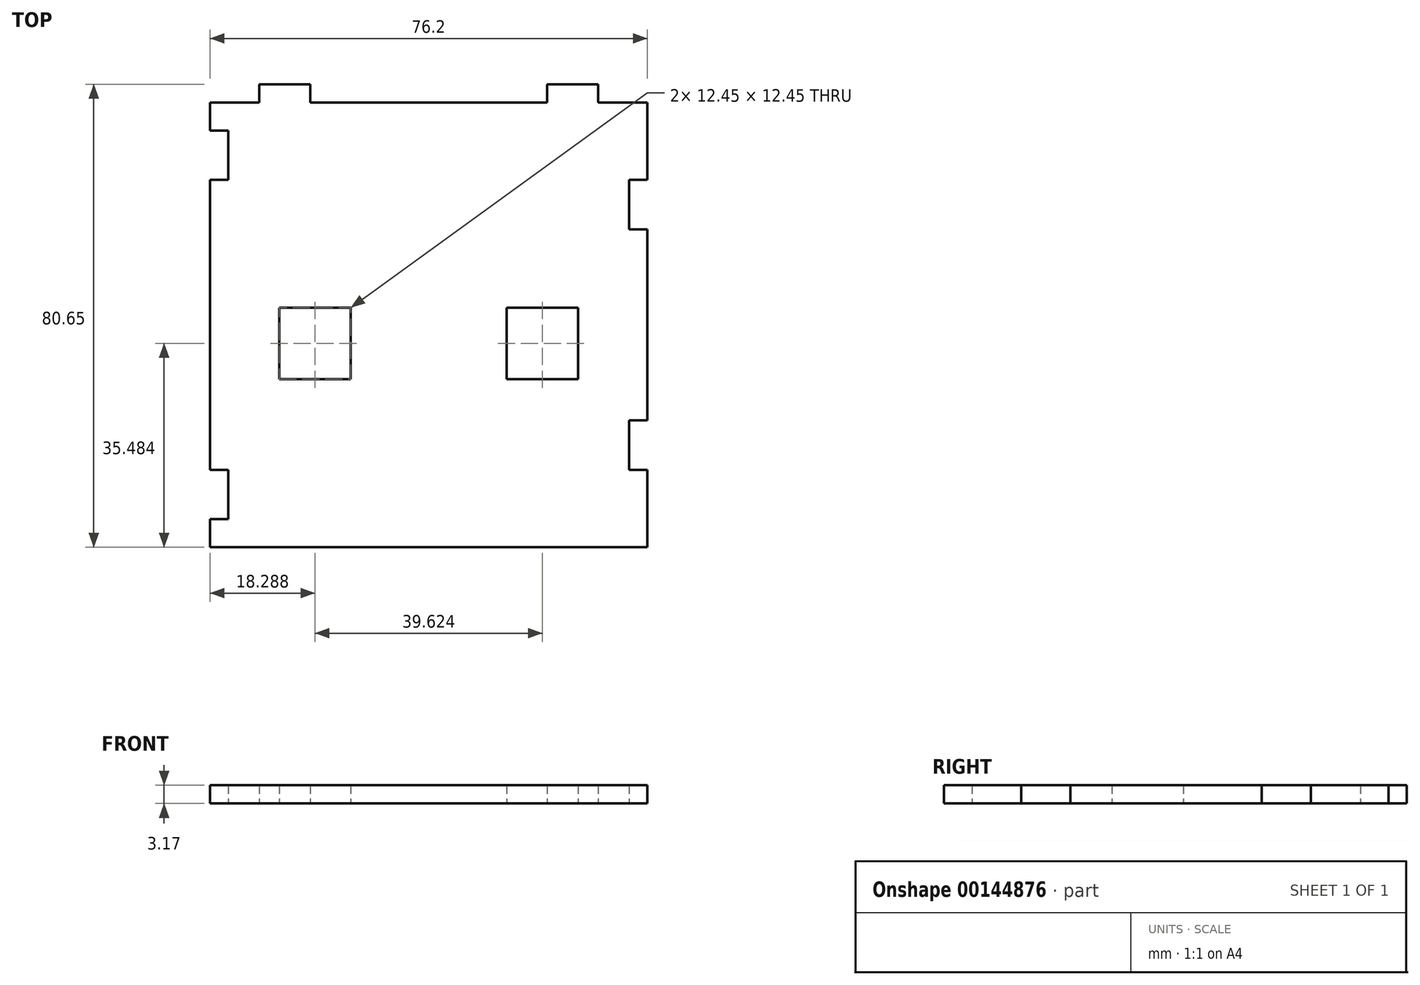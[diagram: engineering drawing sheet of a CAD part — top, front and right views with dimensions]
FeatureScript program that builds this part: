
annotation { "Feature Type Name" : "Feature", "Feature Type Description" : "" }
export const myFeature = defineFeature(function(context is Context, id is Id, definition is map)
    precondition{}
    {
        {
            var Q0;
            Q0=qCreatedBy(makeId("Top.planeOp"),FACE);
            var sketch = newSketch(context, id + "F0", { "sketchPlane" : qUnion([Q0])});
            skLineSegment(sketch, "E0.bottom", {"start": v(-38.1, 41.91) * mm, "end": v(38.1, 41.91) * mm});
            skLineSegment(sketch, "E0.top", {"start": v(-38.1, -35.56) * mm, "end": v(38.1, -35.56) * mm});
            skLineSegment(sketch, "E0.left", {"start": v(-38.1, 41.91) * mm, "end": v(-38.1, -35.56) * mm});
            skLineSegment(sketch, "E0.right", {"start": v(38.1, 41.91) * mm, "end": v(38.1, -35.56) * mm});
            skPoint(sketch, "E1", {"position": v(-29.53, 41.91) * mm});
            skPoint(sketch, "E2", {"position": v(-20.64, 41.91) * mm});
            skPoint(sketch, "E3", {"position": v(0.15, 41.91) * mm});
            skPoint(sketch, "E4", {"position": v(0, 41.91) * mm});
            skPoint(sketch, "E5", {"position": v(20.62, 41.91) * mm});
            skPoint(sketch, "E6", {"position": v(29.51, 41.91) * mm});
            skLineSegment(sketch, "E7", {"start": v(0.15, 41.91) * mm, "end": v(-4.3, 41.91) * mm});
            skPoint(sketch, "E8", {"position": v(4.6, 41.91) * mm});
            skLineSegment(sketch, "E9", {"start": v(0.15, 41.91) * mm, "end": v(4.6, 41.91) * mm});
            skPoint(sketch, "E10", {"position": v(-29.53, -35.56) * mm});
            skPoint(sketch, "E11", {"position": v(-20.64, -35.56) * mm});
            skPoint(sketch, "E12", {"position": v(-4.3, -35.56) * mm});
            skPoint(sketch, "E13", {"position": v(4.6, -35.56) * mm});
            skPoint(sketch, "E14", {"position": v(20.62, -35.56) * mm});
            skPoint(sketch, "E15", {"position": v(29.51, -35.56) * mm});
            skLineSegment(sketch, "E16.bottom", {"start": v(20.62, -35.56) * mm, "end": v(29.2, -35.56) * mm});
            skPoint(sketch, "E17", {"position": v(38.1, 24.13) * mm});
            skPoint(sketch, "E18", {"position": v(38.1, -17.78) * mm});
            skPoint(sketch, "E19", {"position": v(38.1, 3.18) * mm});
            skPoint(sketch, "E20", {"position": v(38.1, 28.42) * mm});
            skPoint(sketch, "E21", {"position": v(38.1, 19.84) * mm});
            skPoint(sketch, "E22", {"position": v(38.1, -13.49) * mm});
            skPoint(sketch, "E23", {"position": v(38.1, -22.07) * mm});
            skLineSegment(sketch, "E24.bottom", {"start": v(38.1, 28.42) * mm, "end": v(34.93, 28.42) * mm});
            skLineSegment(sketch, "E24.top", {"start": v(38.1, 19.84) * mm, "end": v(34.93, 19.84) * mm});
            skLineSegment(sketch, "E24.left", {"start": v(38.1, 28.42) * mm, "end": v(38.1, 19.84) * mm});
            skLineSegment(sketch, "E24.right", {"start": v(34.93, 28.42) * mm, "end": v(34.93, 19.84) * mm});
            skLineSegment(sketch, "E25.bottom", {"start": v(38.1, -13.49) * mm, "end": v(34.93, -13.49) * mm});
            skLineSegment(sketch, "E25.top", {"start": v(38.1, -22.07) * mm, "end": v(34.93, -22.07) * mm});
            skLineSegment(sketch, "E25.left", {"start": v(38.1, -13.49) * mm, "end": v(38.1, -22.07) * mm});
            skLineSegment(sketch, "E25.right", {"start": v(34.93, -13.49) * mm, "end": v(34.93, -22.07) * mm});
            skLineSegment(sketch, "E26.bottom", {"start": v(-38.1, 28.42) * mm, "end": v(-34.92, 28.42) * mm});
            skLineSegment(sketch, "E26.top", {"start": v(-38.1, 37) * mm, "end": v(-34.92, 37) * mm});
            skLineSegment(sketch, "E26.left", {"start": v(-38.1, 28.42) * mm, "end": v(-38.1, 37) * mm});
            skLineSegment(sketch, "E26.right", {"start": v(-34.92, 28.42) * mm, "end": v(-34.92, 37) * mm});
            skLineSegment(sketch, "E27.bottom", {"start": v(-38.1, -22.07) * mm, "end": v(-34.92, -22.07) * mm});
            skLineSegment(sketch, "E27.top", {"start": v(-38.1, -30.66) * mm, "end": v(-34.92, -30.66) * mm});
            skLineSegment(sketch, "E27.left", {"start": v(-38.1, -22.07) * mm, "end": v(-38.1, -30.66) * mm});
            skLineSegment(sketch, "E27.right", {"start": v(-34.93, -22.07) * mm, "end": v(-34.93, -30.66) * mm});
            skLineSegment(sketch, "E28.top", {"start": v(-29.53, 45.09) * mm, "end": v(-20.64, 45.09) * mm});
            skLineSegment(sketch, "E28.left", {"start": v(-29.53, 41.91) * mm, "end": v(-29.53, 45.09) * mm});
            skLineSegment(sketch, "E28.right", {"start": v(-20.64, 41.91) * mm, "end": v(-20.64, 45.09) * mm});
            skLineSegment(sketch, "E29.top", {"start": v(20.62, 45.09) * mm, "end": v(29.51, 45.09) * mm});
            skLineSegment(sketch, "E29.left", {"start": v(20.62, 41.91) * mm, "end": v(20.62, 45.09) * mm});
            skLineSegment(sketch, "E29.right", {"start": v(29.51, 41.91) * mm, "end": v(29.51, 45.09) * mm});
            skLineSegment(sketch, "E30.top", {"start": v(-4.3, 45.09) * mm, "end": v(4.6, 45.09) * mm});
            skLineSegment(sketch, "E30.left", {"start": v(-4.3, 41.91) * mm, "end": v(-4.3, 45.09) * mm});
            skLineSegment(sketch, "E30.right", {"start": v(4.6, 41.91) * mm, "end": v(4.6, 45.09) * mm});
            skLineSegment(sketch, "E31.bottom", {"start": v(-29.53, -35.56) * mm, "end": v(-20.64, -35.56) * mm});
            skLineSegment(sketch, "E31.top", {"start": v(-29.53, -38.73) * mm, "end": v(-20.64, -38.73) * mm});
            skLineSegment(sketch, "E31.left", {"start": v(-29.53, -35.56) * mm, "end": v(-29.53, -38.73) * mm});
            skLineSegment(sketch, "E31.right", {"start": v(-20.64, -35.56) * mm, "end": v(-20.64, -38.73) * mm});
            skLineSegment(sketch, "E32.bottom", {"start": v(-4.3, -35.56) * mm, "end": v(4.6, -35.56) * mm});
            skLineSegment(sketch, "E32.top", {"start": v(-4.3, -38.73) * mm, "end": v(4.6, -38.73) * mm});
            skLineSegment(sketch, "E32.left", {"start": v(-4.3, -35.56) * mm, "end": v(-4.3, -38.73) * mm});
            skLineSegment(sketch, "E32.right", {"start": v(4.6, -35.56) * mm, "end": v(4.6, -38.73) * mm});
            skLineSegment(sketch, "E33.bottom", {"start": v(20.62, -35.56) * mm, "end": v(29.51, -35.56) * mm});
            skLineSegment(sketch, "E33.top", {"start": v(20.62, -38.73) * mm, "end": v(29.51, -38.73) * mm});
            skLineSegment(sketch, "E33.left", {"start": v(20.62, -35.56) * mm, "end": v(20.62, -38.73) * mm});
            skLineSegment(sketch, "E33.right", {"start": v(29.51, -35.56) * mm, "end": v(29.51, -38.73) * mm});
            skLineSegment(sketch, "E34.bottom", {"start": v(13.59, 6.15) * mm, "end": v(26.03, 6.15) * mm});
            skLineSegment(sketch, "E34.top", {"start": v(13.59, -6.3) * mm, "end": v(26.03, -6.3) * mm});
            skLineSegment(sketch, "E34.left", {"start": v(13.59, 6.15) * mm, "end": v(13.59, -6.3) * mm});
            skLineSegment(sketch, "E34.right", {"start": v(26.03, 6.15) * mm, "end": v(26.03, -6.3) * mm});
            skPoint(sketch, "E34.middle", {"position": v(19.81, -0.08) * mm});
            skLineSegment(sketch, "E35.bottom", {"start": v(-26.03, 6.15) * mm, "end": v(-13.59, 6.15) * mm});
            skLineSegment(sketch, "E35.top", {"start": v(-26.03, -6.3) * mm, "end": v(-13.59, -6.3) * mm});
            skLineSegment(sketch, "E35.left", {"start": v(-26.03, 6.15) * mm, "end": v(-26.03, -6.3) * mm});
            skLineSegment(sketch, "E35.right", {"start": v(-13.59, 6.15) * mm, "end": v(-13.59, -6.3) * mm});
            skPoint(sketch, "E35.middle", {"position": v(-19.81, -0.08) * mm});
            skSolve(sketch);
        }
        {
            var Q0;
            Q0=makeQuery(id+"F0.imprint","IMPRINT",FACE,{"disambiguationData":[TD([[makeQuery(id+"F0.imprint","IMPRINT",EDGE,{"derivedFrom":sQuery(id+"F0.wireOp",EDGE,"E0.bottom")}),-1.0]])]});
            var Q1;
            Q1=makeQuery(id+"F0.imprint","IMPRINT",FACE,{"disambiguationData":[TD([[makeQuery(id+"F0.imprint","IMPRINT",EDGE,{"derivedFrom":sQuery(id+"F0.wireOp",EDGE,"E28.top")}),-1.0]])]});
            var Q2;
            Q2=makeQuery(id+"F0.imprint","IMPRINT",FACE,{"disambiguationData":[TD([[makeQuery(id+"F0.imprint","IMPRINT",EDGE,{"derivedFrom":sQuery(id+"F0.wireOp",EDGE,"E7")}),-1.0]])]});
            var Q3;
            Q3=makeQuery(id+"F0.imprint","IMPRINT",FACE,{"disambiguationData":[TD([[makeQuery(id+"F0.imprint","IMPRINT",EDGE,{"derivedFrom":sQuery(id+"F0.wireOp",EDGE,"E29.top")}),-1.0]])]});
            var Q4;
            Q4=makeQuery(id+"F0.imprint","IMPRINT",FACE,{"disambiguationData":[TD([[makeQuery(id+"F0.imprint","IMPRINT",EDGE,{"derivedFrom":sQuery(id+"F0.wireOp",EDGE,"E31.bottom")}),-1.0]])]});
            var Q5;
            Q5=makeQuery(id+"F0.imprint","IMPRINT",FACE,{"disambiguationData":[TD([[makeQuery(id+"F0.imprint","IMPRINT",EDGE,{"derivedFrom":sQuery(id+"F0.wireOp",EDGE,"E32.bottom")}),-1.0]])]});
            var Q6;
            Q6=makeQuery(id+"F0.imprint","IMPRINT",FACE,{"disambiguationData":[TD([[makeQuery(id+"F0.imprint","IMPRINT",EDGE,{"derivedFrom":sQuery(id+"F0.wireOp",EDGE,"E33.bottom")}),-1.0]])]});
            extrude(context, id + "F1", {"entities" : qUnion([Q0, Q1, Q2, Q3, Q4, Q5, Q6]), "depth" : 3.17 * mm});
        }
    });
